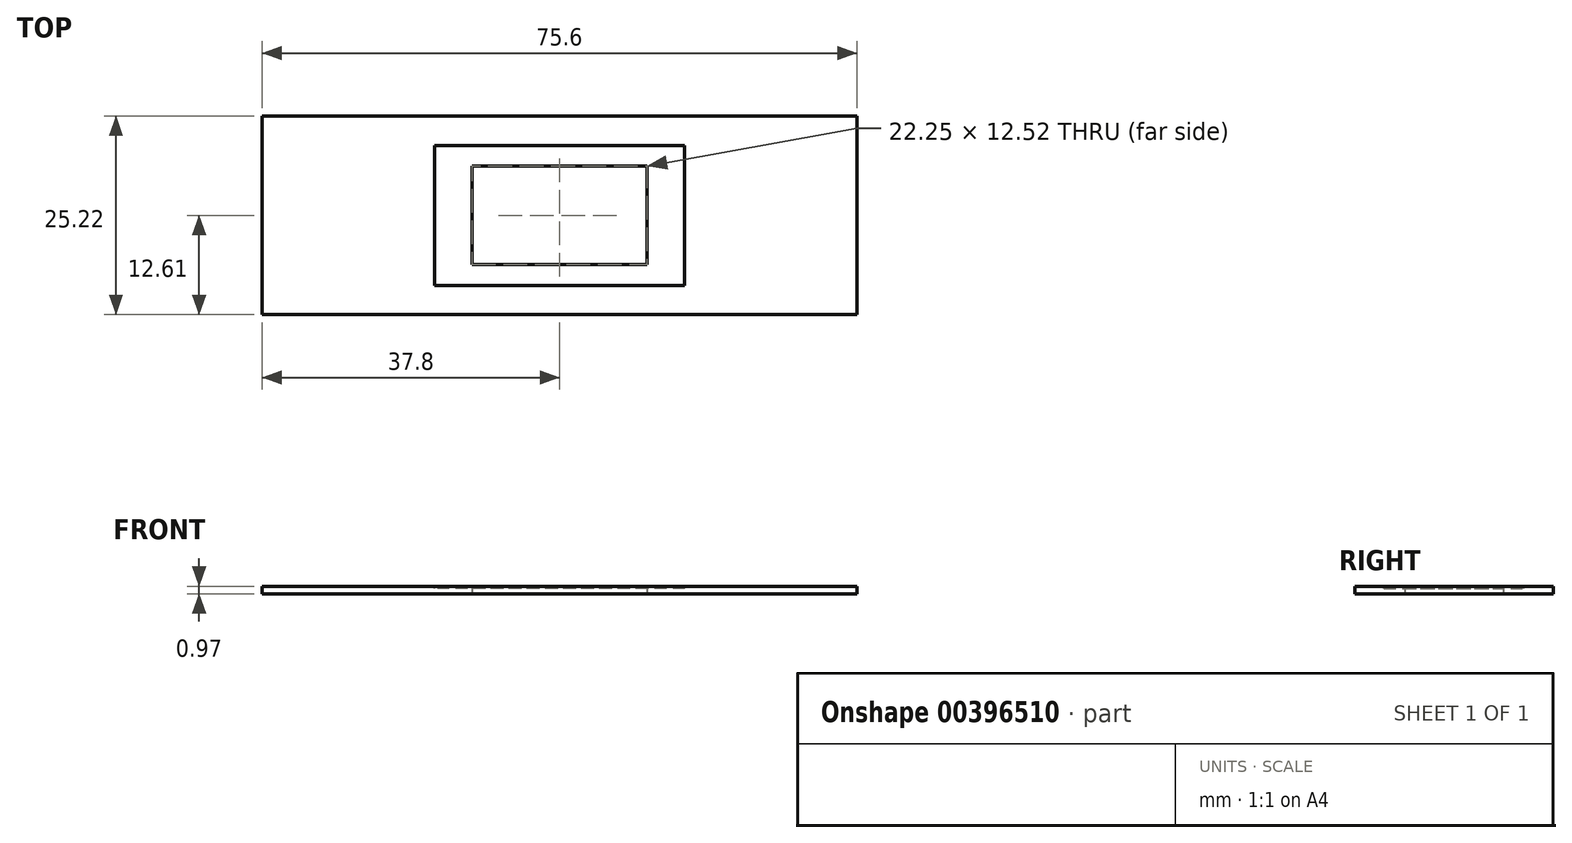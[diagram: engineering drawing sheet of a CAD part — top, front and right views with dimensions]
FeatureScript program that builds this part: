
annotation { "Feature Type Name" : "Feature", "Feature Type Description" : "" }
export const myFeature = defineFeature(function(context is Context, id is Id, definition is map)
    precondition{}
    {
        {
            var Q0;
            Q0=qCreatedBy(makeId("Top.planeOp"),FACE);
            var sketch = newSketch(context, id + "F0", { "sketchPlane" : qUnion([Q0])});
            skLineSegment(sketch, "E0.bottom", {"start": v(-37.8, 12.61) * mm, "end": v(37.8, 12.61) * mm});
            skLineSegment(sketch, "E0.top", {"start": v(-37.8, -12.61) * mm, "end": v(37.8, -12.61) * mm});
            skLineSegment(sketch, "E0.left", {"start": v(-37.8, 12.61) * mm, "end": v(-37.8, -12.61) * mm});
            skLineSegment(sketch, "E0.right", {"start": v(37.8, 12.61) * mm, "end": v(37.8, -12.61) * mm});
            skLineSegment(sketch, "E1", {"start": v(-37.8, 12.61) * mm, "end": v(37.8, -12.61) * mm, "construction": true});
            skLineSegment(sketch, "E2.bottom", {"start": v(11.13, -6.26) * mm, "end": v(-11.13, -6.26) * mm});
            skLineSegment(sketch, "E2.top", {"start": v(11.13, 6.26) * mm, "end": v(-11.13, 6.26) * mm});
            skLineSegment(sketch, "E2.left", {"start": v(11.13, -6.26) * mm, "end": v(11.13, 6.26) * mm});
            skLineSegment(sketch, "E2.right", {"start": v(-11.13, -6.26) * mm, "end": v(-11.13, 6.26) * mm});
            skPoint(sketch, "E2.middle", {"position": v(0, 0) * mm});
            skSolve(sketch);
        }
        {
            var Q0;
            Q0 = qSketchRegion(id + "F0", true);
            extrude(context, id + "F1", {"entities" : qUnion([Q0]), "depth" : 0.97 * mm});
        }
        {
            var Q0;
            Q0=makeQuery(id+"F1.opExtrude","CAP_FACE",FACE,{"disambiguationData":[OSD([sQuery(id+"F0.wireOp",EDGE,"E0.bottom"),sQuery(id+"F0.wireOp",EDGE,"E0.top"),sQuery(id+"F0.wireOp",EDGE,"E0.left"),sQuery(id+"F0.wireOp",EDGE,"E0.right"),sQuery(id+"F0.wireOp",EDGE,"E2.bottom"),sQuery(id+"F0.wireOp",EDGE,"E2.top"),sQuery(id+"F0.wireOp",EDGE,"E2.left"),sQuery(id+"F0.wireOp",EDGE,"E2.right")])],"isStart":false});
            var sketch = newSketch(context, id + "F2", { "sketchPlane" : qUnion([Q0])});
            skLineSegment(sketch, "E3.0", {"start": v(15.87, 8.89) * mm, "end": v(-15.88, 8.89) * mm});
            skLineSegment(sketch, "E3.1", {"start": v(15.87, -8.89) * mm, "end": v(15.87, 8.89) * mm});
            skLineSegment(sketch, "E3.2", {"start": v(15.87, -8.89) * mm, "end": v(-15.88, -8.89) * mm});
            skLineSegment(sketch, "E3.3", {"start": v(-15.88, -8.89) * mm, "end": v(-15.88, 8.89) * mm});
            skLineSegment(sketch, "E4", {"start": v(15.87, -8.89) * mm, "end": v(-15.88, 8.9) * mm, "construction": true});
            skPoint(sketch, "E5", {"position": v(0, 0) * mm});
            skSolve(sketch);
        }
        {
            var Q0;
            Q0 = qSketchRegion(id + "F2", true);
            extrude(context, id + "F3", {"entities" : qUnion([Q0]), "operationType" : NewBodyOperationType.REMOVE, "oppositeDirection" : true, "depth" : 0.3 * mm});
        }
    });
